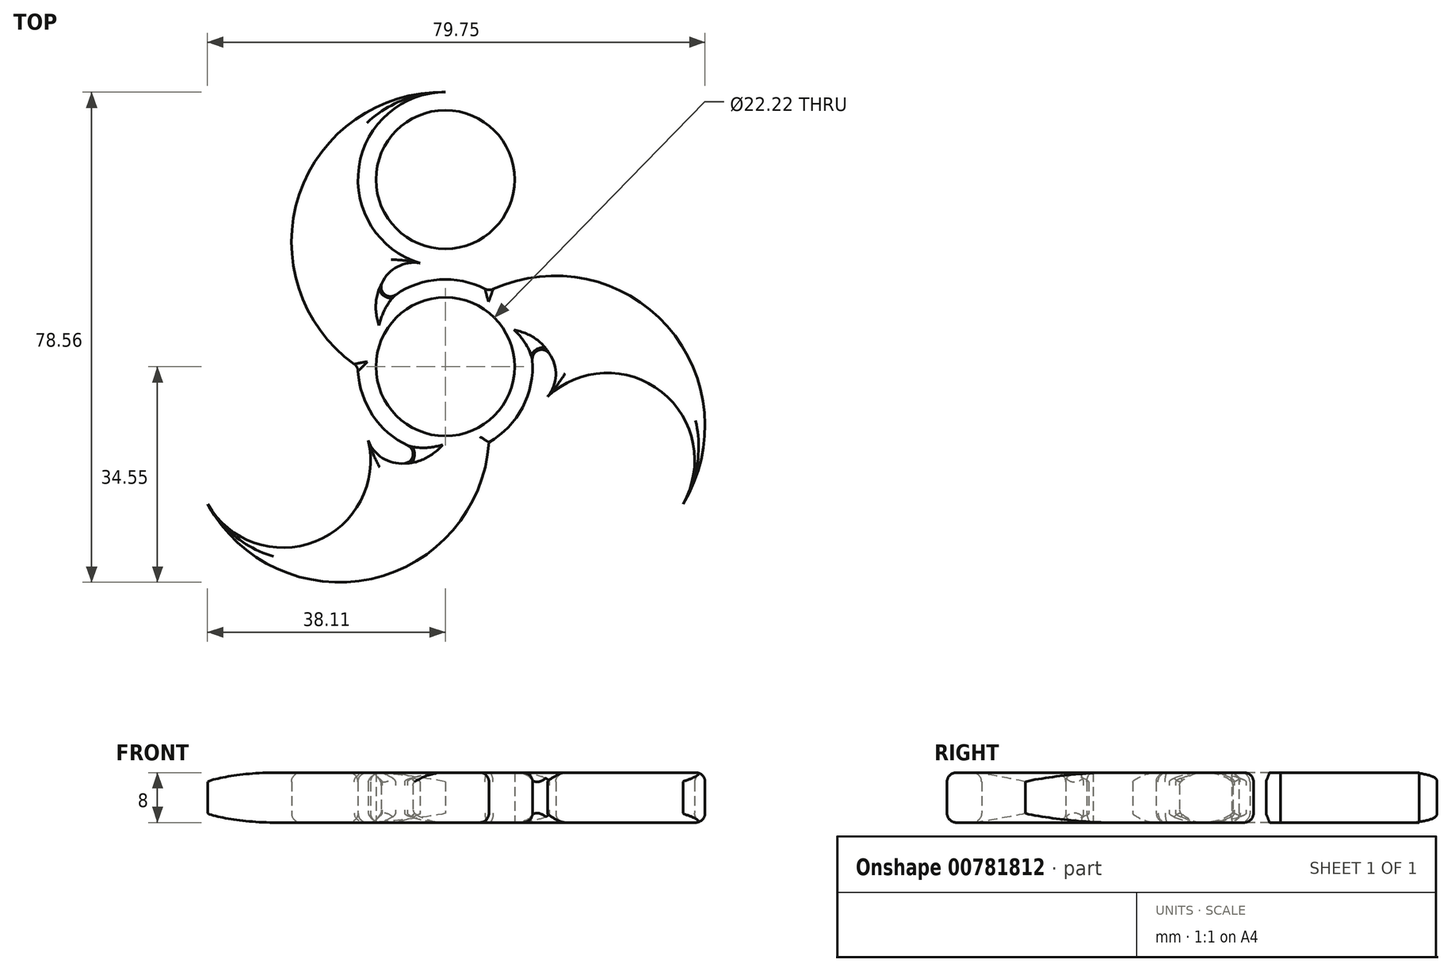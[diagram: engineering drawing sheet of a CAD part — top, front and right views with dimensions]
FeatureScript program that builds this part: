
annotation { "Feature Type Name" : "Feature", "Feature Type Description" : "" }
export const myFeature = defineFeature(function(context is Context, id is Id, definition is map)
    precondition{}
    {
        {
            var Q0;
            Q0=qCreatedBy(makeId("Top.planeOp"),FACE);
            var sketch = newSketch(context, id + "F0", { "sketchPlane" : qUnion([Q0])});
            skCircle(sketch, "E0", {"center": v(0, 0) * mm, "radius": 11.1 * mm});
            skCircle(sketch, "E1", {"center": v(0, 0) * mm, "radius": 14 * mm});
            skLineSegment(sketch, "E2", {"start": v(-20.51, 15) * mm, "end": v(20.51, 15) * mm, "construction": true});
            skLineSegment(sketch, "E3", {"start": v(0, 30) * mm, "end": v(0, 0) * mm, "construction": true});
            skSolve(sketch);
        }
        {
            var Q0;
            Q0=makeQuery(id+"F0.imprint","IMPRINT",FACE,{"disambiguationData":[TD([[makeQuery(id+"F0.imprint","IMPRINT",EDGE,{"derivedFrom":sQuery(id+"F0.wireOp",EDGE,"E0")}),-1.0]])]});
            extrude(context, id + "F1", {"entities" : qUnion([Q0]), "depth" : 8 * mm, "offsetDistance" : 25 * mm});
        }
        {
            var Q0;
            Q0=qCreatedBy(makeId("Top.planeOp"),FACE);
            var sketch = newSketch(context, id + "F2", { "sketchPlane" : qUnion([Q0])});
            skCircle(sketch, "E4.0.0", {"center": v(0, 0) * mm, "radius": 11.1 * mm});
            skCircle(sketch, "E5.0", {"center": v(0, 0) * mm, "radius": 14 * mm});
            skCircle(sketch, "E6.MirrorC", {"center": v(0, 30) * mm, "radius": 14 * mm});
            skCircle(sketch, "E7.MirrorC", {"center": v(0, 30) * mm, "radius": 11.1 * mm});
            skArc(sketch, "E8", {"start": v(0, 44) * mm, "mid": v(-23.52, 27.25) * mm, "end": v(-14, 0) * mm});
            skArc(sketch, "E9", {"start": v(-4.05, 16.6) * mm, "mid": v(-9.27, 14.76) * mm, "end": v(-10.41, 9.36) * mm});
            skSolve(sketch);
        }
        {
            var Q0;
            Q0=qCreatedBy(makeId("Front.planeOp"),FACE);
            var sketch = newSketch(context, id + "F3", { "sketchPlane" : qUnion([Q0])});
            skPoint(sketch, "E10.0", {"position": v(0, 0) * mm});
            skLineSegment(sketch, "E11", {"start": v(0, 0) * mm, "end": v(0, 15.14) * mm, "construction": true});
            skSolve(sketch);
        }
        {
            var Q0;
            Q0=makeQuery(id+"F2.imprint","IMPRINT",FACE,{"disambiguationData":[TD([[makeQuery(id+"F2.imprint","IMPRINT",EDGE,{"derivedFrom":sQuery(id+"F2.wireOp",EDGE,"E7.MirrorC")}),1.0]])]});
            var Q1;
            {var subQ0=sQuery(id+"F2.wireOp",EDGE,"E8");Q1=makeQuery(id+"F2.imprint","IMPRINT",FACE,{"disambiguationData":[TD([[makeQuery(id+"F2.imprint","IMPRINT",EDGE,{"derivedFrom":subQ0}),1.0]])]});}
            extrude(context, id + "F4", {"entities" : qUnion([Q0, Q1]), "depth" : 8 * mm, "offsetDistance" : 25 * mm});
        }
        {
            var Q0;
            Q0=makeQuery(id+"F4.opExtrude","CAP_EDGE",EDGE,{"disambiguationData":[OSD([sQuery(id+"F2.wireOp",EDGE,"E8")])],"isStart":false});
            var Q1;
            Q1=makeQuery(id+"F4.opExtrude","CAP_EDGE",EDGE,{"disambiguationData":[OSD([sQuery(id+"F2.wireOp",EDGE,"E6.MirrorC")])],"isStart":false});
            var Q2;
            Q2=makeQuery(id+"F4.opExtrude","CAP_EDGE",EDGE,{"disambiguationData":[OSD([sQuery(id+"F2.wireOp",EDGE,"E9")])],"isStart":false});
            var Q3;
            Q3=makeQuery(id+"F4.opExtrude","CAP_EDGE",EDGE,{"disambiguationData":[OSD([sQuery(id+"F2.wireOp",EDGE,"E8")])],"isStart":true});
            var Q4;
            Q4=makeQuery(id+"F4.opExtrude","CAP_EDGE",EDGE,{"disambiguationData":[OSD([sQuery(id+"F2.wireOp",EDGE,"E6.MirrorC")])],"isStart":true});
            var Q5;
            Q5=makeQuery(id+"F4.opExtrude","CAP_EDGE",EDGE,{"disambiguationData":[OSD([sQuery(id+"F2.wireOp",EDGE,"E9")])],"isStart":true});
            fillet(context, id + "F5", {"entities" : qUnion([Q0, Q1, Q2, Q3, Q4, Q5]), "radius" : 1.5 * mm, "tangentPropagation" : true, "allowEdgeOverflow" : false});
        }
        {
            var Q0;
            Q0=makeQuery(id+"F4.opExtrude","SWEPT_BODY",BODY,{"disambiguationData":[OSD([sQuery(id+"F2.wireOp",EDGE,"E5.0"),sQuery(id+"F2.wireOp",EDGE,"E6.MirrorC"),sQuery(id+"F2.wireOp",EDGE,"E7.MirrorC"),sQuery(id+"F2.wireOp",EDGE,"E8"),sQuery(id+"F2.wireOp",EDGE,"E9")])]});
            var Q1;
            Q1=sQuery(id+"F3.wireOp",EDGE,"E11");
            circularPattern(context, id + "F6", {"entities" : qUnion([Q0]), "axis" : qUnion([Q1]), "angle" : 360 * degree, "instanceCount" : 3, "equalSpace" : true});
        }
        {
            var Q0;
            Q0=makeQuery(id+"F4.opExtrude","SWEPT_BODY",BODY,{"disambiguationData":[OSD([sQuery(id+"F2.wireOp",EDGE,"E5.0"),sQuery(id+"F2.wireOp",EDGE,"E6.MirrorC"),sQuery(id+"F2.wireOp",EDGE,"E7.MirrorC"),sQuery(id+"F2.wireOp",EDGE,"E8"),sQuery(id+"F2.wireOp",EDGE,"E9")])]});
            var Q1;
            Q1=makeQuery(id+"F6.opPattern","COPY",BODY,{"derivedFrom":makeQuery(id+"F4.opExtrude","SWEPT_BODY",BODY,{"disambiguationData":[OSD([sQuery(id+"F2.wireOp",EDGE,"E5.0"),sQuery(id+"F2.wireOp",EDGE,"E6.MirrorC"),sQuery(id+"F2.wireOp",EDGE,"E7.MirrorC"),sQuery(id+"F2.wireOp",EDGE,"E8"),sQuery(id+"F2.wireOp",EDGE,"E9")])]}),"instanceName":"2"});
            var Q2;
            Q2=makeQuery(id+"F6.opPattern","COPY",BODY,{"derivedFrom":makeQuery(id+"F4.opExtrude","SWEPT_BODY",BODY,{"disambiguationData":[OSD([sQuery(id+"F2.wireOp",EDGE,"E5.0"),sQuery(id+"F2.wireOp",EDGE,"E6.MirrorC"),sQuery(id+"F2.wireOp",EDGE,"E7.MirrorC"),sQuery(id+"F2.wireOp",EDGE,"E8"),sQuery(id+"F2.wireOp",EDGE,"E9")])]}),"instanceName":"1"});
            var Q3;
            Q3=makeQuery(id+"F1.opExtrude","SWEPT_BODY",BODY,{"disambiguationData":[OSD([sQuery(id+"F0.wireOp",EDGE,"E0"),sQuery(id+"F0.wireOp",EDGE,"E1")])]});
            booleanBodies(context, id + "F7", {"operationType" : BooleanOperationType.UNION, "tools" : qUnion([Q0, Q1, Q2, Q3])});
        }
        {
            var Q0;
            {var subQ1=sQuery(id+"F2.wireOp",EDGE,"E8");var subQ3=sQuery(id+"F0.wireOp",EDGE,"E1");Q0=makeQuery(id+"F7.opBoolean","SPLIT",EDGE,{"disambiguationData":[TD([makeQuery(id+"F5.opFillet","BLEND_FACE",FACE,{"disambiguationData":[OSD([subQ1]),TDD([makeQuery(id+"F4.opExtrude","CAP_EDGE",EDGE,{"disambiguationData":[OSD([subQ1])],"isStart":false})])]})])],"derivedFrom":makeQuery(id+"F1.opExtrude","CAP_EDGE",EDGE,{"disambiguationData":[OSD([subQ3])],"isStart":false})});}
            var Q1;
            {var subQ0=sQuery(id+"F2.wireOp",EDGE,"E9");var subQ1=sQuery(id+"F0.wireOp",EDGE,"E1");Q1=makeQuery(id+"F7.opBoolean","SPLIT",EDGE,{"disambiguationData":[TD([makeQuery(id+"F5.opFillet","BLEND_FACE",FACE,{"disambiguationData":[OSD([subQ0]),TDD([makeQuery(id+"F4.opExtrude","CAP_EDGE",EDGE,{"disambiguationData":[OSD([subQ0])],"isStart":false})])]})])],"derivedFrom":makeQuery(id+"F1.opExtrude","CAP_EDGE",EDGE,{"disambiguationData":[OSD([subQ1])],"isStart":false})});}
            var Q2;
            {var subQ0=sQuery(id+"F2.wireOp",EDGE,"E8");var subQ3=sQuery(id+"F0.wireOp",EDGE,"E1");Q2=makeQuery(id+"F7.opBoolean","SPLIT",EDGE,{"disambiguationData":[TD([makeQuery(id+"F6.opPattern","COPY",FACE,{"derivedFrom":makeQuery(id+"F5.opFillet","BLEND_FACE",FACE,{"disambiguationData":[OSD([subQ0]),TDD([makeQuery(id+"F4.opExtrude","CAP_EDGE",EDGE,{"disambiguationData":[OSD([subQ0])],"isStart":false})])]}),"instanceName":"1"})])],"derivedFrom":makeQuery(id+"F1.opExtrude","CAP_EDGE",EDGE,{"disambiguationData":[OSD([subQ3])],"isStart":false})});}
            var Q3;
            {var subQ0=sQuery(id+"F2.wireOp",EDGE,"E8");var subQ3=sQuery(id+"F0.wireOp",EDGE,"E1");Q3=makeQuery(id+"F7.opBoolean","SPLIT",EDGE,{"disambiguationData":[TD([makeQuery(id+"F5.opFillet","BLEND_FACE",FACE,{"disambiguationData":[OSD([subQ0]),TDD([makeQuery(id+"F4.opExtrude","CAP_EDGE",EDGE,{"disambiguationData":[OSD([subQ0])],"isStart":true})])]})])],"derivedFrom":makeQuery(id+"F1.opExtrude","CAP_EDGE",EDGE,{"disambiguationData":[OSD([subQ3])],"isStart":true})});}
            var Q4;
            {var subQ0=sQuery(id+"F2.wireOp",EDGE,"E9");var subQ3=sQuery(id+"F0.wireOp",EDGE,"E1");Q4=makeQuery(id+"F7.opBoolean","SPLIT",EDGE,{"disambiguationData":[TD([makeQuery(id+"F5.opFillet","BLEND_FACE",FACE,{"disambiguationData":[OSD([subQ0]),TDD([makeQuery(id+"F4.opExtrude","CAP_EDGE",EDGE,{"disambiguationData":[OSD([subQ0])],"isStart":true})])]})])],"derivedFrom":makeQuery(id+"F1.opExtrude","CAP_EDGE",EDGE,{"disambiguationData":[OSD([subQ3])],"isStart":true})});}
            var Q5;
            {var subQ0=sQuery(id+"F2.wireOp",EDGE,"E8");var subQ3=sQuery(id+"F0.wireOp",EDGE,"E1");Q5=makeQuery(id+"F7.opBoolean","SPLIT",EDGE,{"disambiguationData":[TD([makeQuery(id+"F6.opPattern","COPY",FACE,{"derivedFrom":makeQuery(id+"F5.opFillet","BLEND_FACE",FACE,{"disambiguationData":[OSD([subQ0]),TDD([makeQuery(id+"F4.opExtrude","CAP_EDGE",EDGE,{"disambiguationData":[OSD([subQ0])],"isStart":true})])]}),"instanceName":"1"})])],"derivedFrom":makeQuery(id+"F1.opExtrude","CAP_EDGE",EDGE,{"disambiguationData":[OSD([subQ3])],"isStart":true})});}
            fillet(context, id + "F8", {"entities" : qUnion([Q0, Q1, Q2, Q3, Q4, Q5]), "radius" : 1.5 * mm, "tangentPropagation" : true, "allowEdgeOverflow" : false});
        }
        {
            var Q0;
            Q0=makeQuery(id+"F6.opPattern","COPY",EDGE,{"derivedFrom":makeQuery(id+"F4.opExtrude","SWEPT_EDGE",EDGE,{"disambiguationData":[OSD([sQuery(id+"F2.wireOp",EDGE,"E5.0"),sQuery(id+"F2.wireOp",EDGE,"E8")])]}),"instanceName":"1"});
            var Q1;
            Q1=makeQuery(id+"F6.opPattern","COPY",EDGE,{"derivedFrom":makeQuery(id+"F4.opExtrude","SWEPT_EDGE",EDGE,{"disambiguationData":[OSD([sQuery(id+"F2.wireOp",EDGE,"E5.0"),sQuery(id+"F2.wireOp",EDGE,"E9")])]}),"instanceName":"1"});
            var Q2;
            {var subQ0=sQuery(id+"F2.wireOp",EDGE,"E9");var subQ1=makeQuery(id+"F6.opPattern","COPY",FACE,{"derivedFrom":makeQuery(id+"F5.opFillet","BLEND_FACE",FACE,{"disambiguationData":[OSD([subQ0]),TDD([makeQuery(id+"F4.opExtrude","CAP_EDGE",EDGE,{"disambiguationData":[OSD([subQ0])],"isStart":false})])]}),"instanceName":"1"});var subQ2=sQuery(id+"F2.wireOp",EDGE,"E8");var subQ4=sQuery(id+"F0.wireOp",EDGE,"E1");Q2=makeQuery(id+"F8.opFillet","BLEND_EDGE",EDGE,{"blendedFrom":[makeQuery(id+"F7.opBoolean","SPLIT",EDGE,{"disambiguationData":[TD([makeQuery(id+"F5.opFillet","BLEND_FACE",FACE,{"disambiguationData":[OSD([subQ2]),TDD([makeQuery(id+"F4.opExtrude","CAP_EDGE",EDGE,{"disambiguationData":[OSD([subQ2])],"isStart":false})])]})])],"derivedFrom":makeQuery(id+"F1.opExtrude","CAP_EDGE",EDGE,{"disambiguationData":[OSD([subQ4])],"isStart":false})}),subQ1],"blendedInto":[subQ1]});}
            var Q3;
            {var subQ0=sQuery(id+"F2.wireOp",EDGE,"E8");var subQ1=makeQuery(id+"F5.opFillet","BLEND_FACE",FACE,{"disambiguationData":[OSD([subQ0]),TDD([makeQuery(id+"F4.opExtrude","CAP_EDGE",EDGE,{"disambiguationData":[OSD([subQ0])],"isStart":false})])]});var subQ4=sQuery(id+"F0.wireOp",EDGE,"E1");Q3=makeQuery(id+"F8.opFillet","BLEND_EDGE",EDGE,{"blendedFrom":[makeQuery(id+"F7.opBoolean","SPLIT",EDGE,{"disambiguationData":[TD([subQ1])],"derivedFrom":makeQuery(id+"F1.opExtrude","CAP_EDGE",EDGE,{"disambiguationData":[OSD([subQ4])],"isStart":false})}),subQ1],"blendedInto":[subQ1]});}
            var Q4;
            {var subQ0=sQuery(id+"F2.wireOp",EDGE,"E9");var subQ1=makeQuery(id+"F5.opFillet","BLEND_FACE",FACE,{"disambiguationData":[OSD([subQ0]),TDD([makeQuery(id+"F4.opExtrude","CAP_EDGE",EDGE,{"disambiguationData":[OSD([subQ0])],"isStart":false})])]});var subQ2=sQuery(id+"F0.wireOp",EDGE,"E1");Q4=makeQuery(id+"F8.opFillet","BLEND_EDGE",EDGE,{"blendedFrom":[makeQuery(id+"F7.opBoolean","SPLIT",EDGE,{"disambiguationData":[TD([subQ1])],"derivedFrom":makeQuery(id+"F1.opExtrude","CAP_EDGE",EDGE,{"disambiguationData":[OSD([subQ2])],"isStart":false})}),subQ1],"blendedInto":[subQ1]});}
            var Q5;
            {var subQ0=sQuery(id+"F2.wireOp",EDGE,"E8");var subQ1=makeQuery(id+"F6.opPattern","COPY",FACE,{"derivedFrom":makeQuery(id+"F5.opFillet","BLEND_FACE",FACE,{"disambiguationData":[OSD([subQ0]),TDD([makeQuery(id+"F4.opExtrude","CAP_EDGE",EDGE,{"disambiguationData":[OSD([subQ0])],"isStart":false})])]}),"instanceName":"2"});var subQ2=sQuery(id+"F2.wireOp",EDGE,"E9");var subQ3=sQuery(id+"F0.wireOp",EDGE,"E1");Q5=makeQuery(id+"F8.opFillet","BLEND_EDGE",EDGE,{"blendedFrom":[makeQuery(id+"F7.opBoolean","SPLIT",EDGE,{"disambiguationData":[TD([makeQuery(id+"F5.opFillet","BLEND_FACE",FACE,{"disambiguationData":[OSD([subQ2]),TDD([makeQuery(id+"F4.opExtrude","CAP_EDGE",EDGE,{"disambiguationData":[OSD([subQ2])],"isStart":false})])]})])],"derivedFrom":makeQuery(id+"F1.opExtrude","CAP_EDGE",EDGE,{"disambiguationData":[OSD([subQ3])],"isStart":false})}),subQ1],"blendedInto":[subQ1]});}
            var Q6;
            {var subQ0=sQuery(id+"F2.wireOp",EDGE,"E9");var subQ1=makeQuery(id+"F6.opPattern","COPY",FACE,{"derivedFrom":makeQuery(id+"F5.opFillet","BLEND_FACE",FACE,{"disambiguationData":[OSD([subQ0]),TDD([makeQuery(id+"F4.opExtrude","CAP_EDGE",EDGE,{"disambiguationData":[OSD([subQ0])],"isStart":false})])]}),"instanceName":"2"});var subQ2=sQuery(id+"F2.wireOp",EDGE,"E8");var subQ4=sQuery(id+"F0.wireOp",EDGE,"E1");Q6=makeQuery(id+"F8.opFillet","BLEND_EDGE",EDGE,{"blendedFrom":[makeQuery(id+"F7.opBoolean","SPLIT",EDGE,{"disambiguationData":[TD([makeQuery(id+"F6.opPattern","COPY",FACE,{"derivedFrom":makeQuery(id+"F5.opFillet","BLEND_FACE",FACE,{"disambiguationData":[OSD([subQ2]),TDD([makeQuery(id+"F4.opExtrude","CAP_EDGE",EDGE,{"disambiguationData":[OSD([subQ2])],"isStart":false})])]}),"instanceName":"1"})])],"derivedFrom":makeQuery(id+"F1.opExtrude","CAP_EDGE",EDGE,{"disambiguationData":[OSD([subQ4])],"isStart":false})}),subQ1],"blendedInto":[subQ1]});}
            fillet(context, id + "F9", {"entities" : qUnion([Q0, Q1, Q2, Q3, Q4, Q5, Q6]), "radius" : 1.5 * mm, "tangentPropagation" : true, "allowEdgeOverflow" : false});
        }
    });
